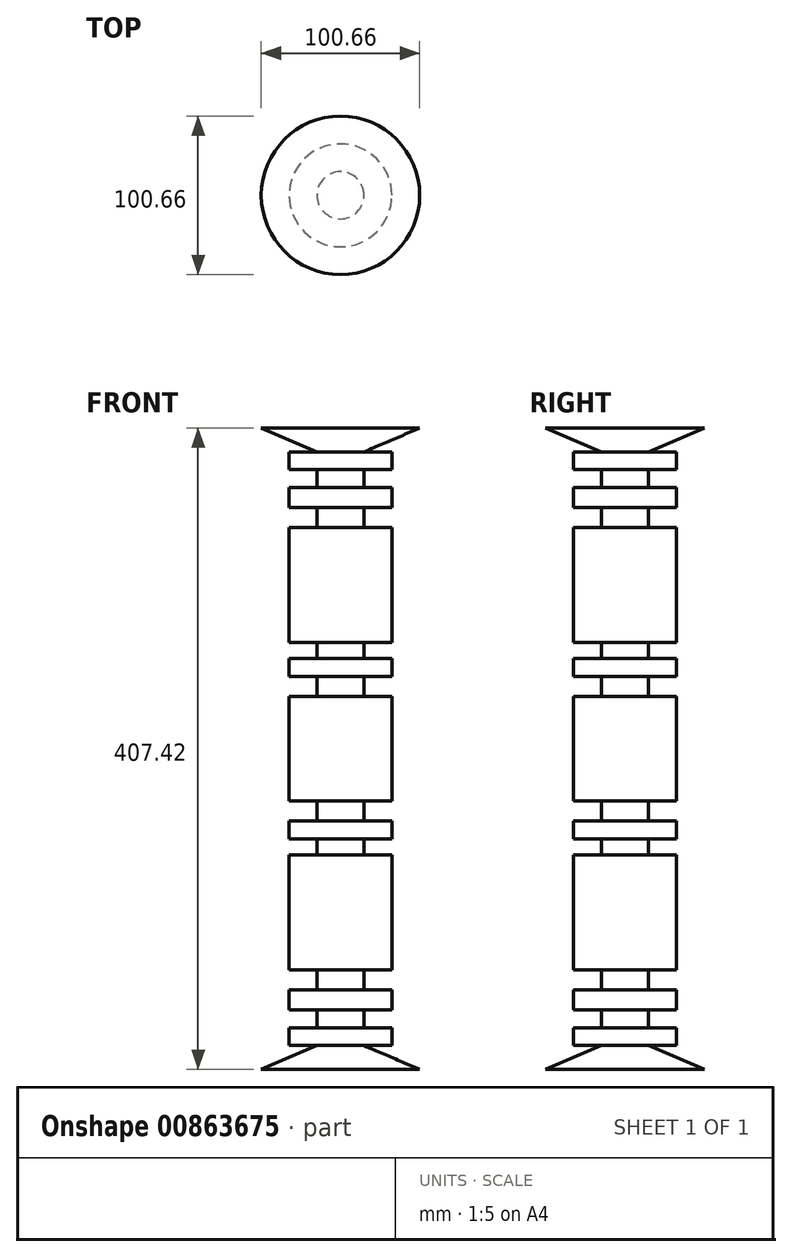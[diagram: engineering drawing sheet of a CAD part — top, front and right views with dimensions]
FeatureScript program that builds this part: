
annotation { "Feature Type Name" : "Feature", "Feature Type Description" : "" }
export const myFeature = defineFeature(function(context is Context, id is Id, definition is map)
    precondition{}
    {
        {
            var Q0;
            Q0=qCreatedBy(makeId("Front.planeOp"),FACE);
            var sketch = newSketch(context, id + "F0", { "sketchPlane" : qUnion([Q0])});
            skLineSegment(sketch, "E0", {"start": v(0, 0) * mm, "end": v(0, -203.71) * mm});
            skLineSegment(sketch, "E1", {"start": v(0, -203.71) * mm, "end": v(50.33, -203.71) * mm});
            skLineSegment(sketch, "E2", {"start": v(50.33, -203.71) * mm, "end": v(14.98, -188.56) * mm});
            skLineSegment(sketch, "E3", {"start": v(14.98, -188.56) * mm, "end": v(32.66, -188.56) * mm});
            skPoint(sketch, "E3.endSnap0", {"position": v(32.66, -196.14) * mm});
            skLineSegment(sketch, "E4", {"start": v(32.66, -188.56) * mm, "end": v(32.66, -177.2) * mm});
            skLineSegment(sketch, "E5", {"start": v(32.66, -177.2) * mm, "end": v(14.98, -177.2) * mm});
            skLineSegment(sketch, "E6", {"start": v(14.98, -177.2) * mm, "end": v(14.98, -165.84) * mm});
            skLineSegment(sketch, "E7", {"start": v(14.98, -165.84) * mm, "end": v(32.66, -165.84) * mm});
            skLineSegment(sketch, "E8", {"start": v(32.66, -165.84) * mm, "end": v(32.66, -153.21) * mm});
            skLineSegment(sketch, "E9", {"start": v(32.66, -153.21) * mm, "end": v(14.98, -153.21) * mm});
            skLineSegment(sketch, "E10", {"start": v(14.98, -153.21) * mm, "end": v(14.98, -140.59) * mm});
            skLineSegment(sketch, "E11", {"start": v(14.98, -140.59) * mm, "end": v(32.66, -140.59) * mm});
            skLineSegment(sketch, "E12", {"start": v(32.66, -140.59) * mm, "end": v(32.66, -67.36) * mm});
            skLineSegment(sketch, "E13", {"start": v(32.66, -67.36) * mm, "end": v(14.98, -67.36) * mm});
            skLineSegment(sketch, "E14", {"start": v(14.98, -67.36) * mm, "end": v(14.98, -57.26) * mm});
            skLineSegment(sketch, "E15", {"start": v(14.98, -57.26) * mm, "end": v(32.66, -57.26) * mm});
            skLineSegment(sketch, "E16", {"start": v(32.66, -57.26) * mm, "end": v(32.66, -45.9) * mm});
            skLineSegment(sketch, "E17", {"start": v(32.66, -45.9) * mm, "end": v(14.98, -45.9) * mm});
            skLineSegment(sketch, "E18", {"start": v(14.98, -45.9) * mm, "end": v(14.98, -33.28) * mm});
            skLineSegment(sketch, "E19", {"start": v(14.98, -33.28) * mm, "end": v(32.66, -33.28) * mm});
            skLineSegment(sketch, "E20", {"start": v(32.66, -33.28) * mm, "end": v(32.66, 0) * mm});
            skLineSegment(sketch, "E21", {"start": v(32.66, 0) * mm, "end": v(0, 0) * mm});
            skLineSegment(sketch, "E22.MirrorCS", {"start": v(14.98, 177.2) * mm, "end": v(14.98, 165.84) * mm});
            skLineSegment(sketch, "E23.MirrorCS", {"start": v(14.98, 57.26) * mm, "end": v(32.66, 57.26) * mm});
            skLineSegment(sketch, "E24.MirrorCS", {"start": v(32.66, 67.36) * mm, "end": v(14.98, 67.36) * mm});
            skLineSegment(sketch, "E25.MirrorCS", {"start": v(32.66, 188.56) * mm, "end": v(32.66, 177.2) * mm});
            skLineSegment(sketch, "E26.MirrorCS", {"start": v(14.98, 165.84) * mm, "end": v(32.66, 165.84) * mm});
            skLineSegment(sketch, "E27.MirrorCS", {"start": v(32.66, 165.84) * mm, "end": v(32.66, 153.21) * mm});
            skLineSegment(sketch, "E28.MirrorCS", {"start": v(14.98, 188.56) * mm, "end": v(32.66, 188.56) * mm});
            skLineSegment(sketch, "E29.MirrorCS", {"start": v(32.66, 177.2) * mm, "end": v(14.98, 177.2) * mm});
            skLineSegment(sketch, "E30.MirrorCS", {"start": v(32.66, 57.26) * mm, "end": v(32.66, 45.9) * mm});
            skLineSegment(sketch, "E31.MirrorCS", {"start": v(32.66, 153.21) * mm, "end": v(14.98, 153.21) * mm});
            skLineSegment(sketch, "E32.MirrorCS", {"start": v(32.66, 45.9) * mm, "end": v(14.98, 45.9) * mm});
            skLineSegment(sketch, "E33.MirrorCS", {"start": v(14.98, 153.21) * mm, "end": v(14.98, 140.59) * mm});
            skLineSegment(sketch, "E34.MirrorCS", {"start": v(50.33, 203.71) * mm, "end": v(14.98, 188.56) * mm});
            skLineSegment(sketch, "E35.MirrorCS", {"start": v(14.98, 33.28) * mm, "end": v(32.66, 33.28) * mm});
            skLineSegment(sketch, "E36.MirrorCS", {"start": v(14.98, 67.36) * mm, "end": v(14.98, 57.26) * mm});
            skLineSegment(sketch, "E37.MirrorCS", {"start": v(14.98, 140.59) * mm, "end": v(32.66, 140.59) * mm});
            skLineSegment(sketch, "E38.MirrorCS", {"start": v(14.98, 45.9) * mm, "end": v(14.98, 33.28) * mm});
            skLineSegment(sketch, "E39.MirrorCS", {"start": v(0, 203.71) * mm, "end": v(50.33, 203.71) * mm});
            skLineSegment(sketch, "E40.MirrorCS", {"start": v(32.66, 140.59) * mm, "end": v(32.66, 67.36) * mm});
            skLineSegment(sketch, "E41.MirrorCS", {"start": v(0, 0) * mm, "end": v(0, 203.71) * mm});
            skPoint(sketch, "E42.MirrorP", {"position": v(32.66, 196.14) * mm});
            skLineSegment(sketch, "E43.MirrorCS", {"start": v(32.66, 33.28) * mm, "end": v(32.66, 0) * mm});
            skSolve(sketch);
        }
        {
            var Q0;
            Q0=makeQuery(id+"F0.imprint","IMPRINT",FACE,{"disambiguationData":[TD([[makeQuery(id+"F0.imprint","IMPRINT",EDGE,{"derivedFrom":sQuery(id+"F0.wireOp",EDGE,"E21")}),-1.0]])]});
            var Q1;
            Q1=makeQuery(id+"F0.imprint","IMPRINT",FACE,{"disambiguationData":[TD([[makeQuery(id+"F0.imprint","IMPRINT",EDGE,{"derivedFrom":sQuery(id+"F0.wireOp",EDGE,"E0")}),1.0]])]});
            var Q2;
            Q2=sQuery(id+"F0.wireOp",EDGE,"E0");
            revolve(context, id + "F1", {"surfaceOperationType" : NewSurfaceOperationType.NEW, "entities" : qUnion([Q0, Q1]), "axis" : qUnion([Q2]), "revolveType" : RevolveType.FULL});
        }
    });
